# Revit family: СЕРИЯ ЖКХ
name_source: partatom
category: Осветительные приборы
revit_build: Autodesk Revit 2016 (Build: 20151007_0715(x64)
units: mm (PartAtom-declared; Revit-internal decimal feet)

## family parameters
Источник света = Да
Общий = Нет
Основа = Грань
При загрузке вырезать с полостями = Да
Размер круглого соединителя = Использовать диаметр
Тип детали = Нормальный
Точка расчета площади = Нет

## types (4) — shared parameters
ADSK_Единица измерения = Шт.
ADSK_Завод-изготовитель = ГК «Вартон»
ADSK_Количество фаз = 1
ADSK_Количество фаз числовое = 1
ADSK_Коэффициент мощности = 0.97
ADSK_Масса = 0.38
ADSK_Напряжение = 220 В
ADSK_Номинальная мощность = 0 кВт
ADSK_Полная мощность = 0 кВ·А
ADSK_Размер_Высота = 52 мм
ADSK_Размер_Длина = 224 мм
ADSK_Размер_Ширина = 90 мм
ADSK_Ток = 0 А
ADSK_Энергоэффективность = 0 лм/Вт
IP Class = IP65
URL = http://varton.ru
Блок аварийного питания = Нет
Видимая форма излучения при визуализации = Нет
Группа модели = Светильники
Изготовитель = ГК «Вартон»
Излучение по длине прямоугольника = 224 мм
Излучение по ширине прямоугольника = 90 мм
Класс Защиты = II
Класс пожароопасности = нет
Климатическая зона = УХЛ1
Корпус = ABS-пластик
Область использования = Рекомендован для внутреннего освещения подъездов, лестничных пролетов и других объектов жилищно-коммунальной инфраструктуры
Плафон = Плафон самосвечение
Полная установленная мощность = 0 кВ·А
Разработчик = ООО ПРОРУБИМ
Разработчик (телефон) = +7 (495) 649-85-43
Разработчик модели (URL) = http://prorubim.com
Светофильтр = 16777215
Смещение цветовой температуры при затухании лампы = <Нет>
Тип ИС = LED
УОИС = УОИС : Светильник светодиодный
Угол наклона = -90.00°
Файл фотометрической сетки = V1-U0-00006-21000-6500850-1740.ies
zero-valued in all types: Отметка по умолчанию

## per-type parameters (varying)
| type | ADSK_Наименование | Описание | Тип продукции |
| V1-U0-00006-21000-6500850 | Светодиодный светильник ВАРТОН ЖКХ серия IP65 224*90*52 мм антивандальный 8ВТ 5000К 1/20 | Светодиодный светильник ВАРТОН ЖКХ серия IP65 224*90*52 мм антивандальный 8ВТ 5000К 1/20 | Светодиодный светильник ВАРТОН ЖКХ серия IP65 224*90*52 мм антивандальный 8ВТ 5000К 1/20 |
| V1-U0-00006-21N00-6501250 | Светодиодный светильник ВАРТОН ЖКХ серия IP65 224*90*52 мм антивандальный 12ВТ 5000К 1/20 | Светодиодный светильник ВАРТОН ЖКХ серия IP65 224*90*52 мм антивандальный 12ВТ 5000К 1/20 | Светодиодный светильник ВАРТОН ЖКХ серия IP65 224*90*52 мм антивандальный 12ВТ 5000К 1/20 |
| V1-U0-00006-21000-6501250 | Светодиодный светильник ВАРТОН ЖКХ серия IP65 224*90*52 мм антивандальный 12ВТ 5000К 1/20 | Светодиодный светильник ВАРТОН ЖКХ серия IP65 224*90*52 мм антивандальный 12ВТ 5000К 1/20 | Светодиодный светильник ВАРТОН ЖКХ серия IP65 224*90*52 мм антивандальный 12ВТ 5000К 1/20 |
| V1-U0-00006-21S00-6501250 | Светодиодный светильник ВАРТОН ЖКХ серия IP65 224*90*52 мм антивандальный 12ВТ 5000К 1/20 | Светодиодный светильник ВАРТОН ЖКХ серия IP65 224*90*52 мм антивандальный 12ВТ 5000К 1/20 | Светодиодный светильник ВАРТОН ЖКХ серия IP65 224*90*52 мм антивандальный 12ВТ 5000К 1/20 |

note: column(s) folded — value = type name in every type: ADSK_Код изделия

## geometry (parser evidence)
native form markers: Blend x2
no freeform markers — native parametric forms only
